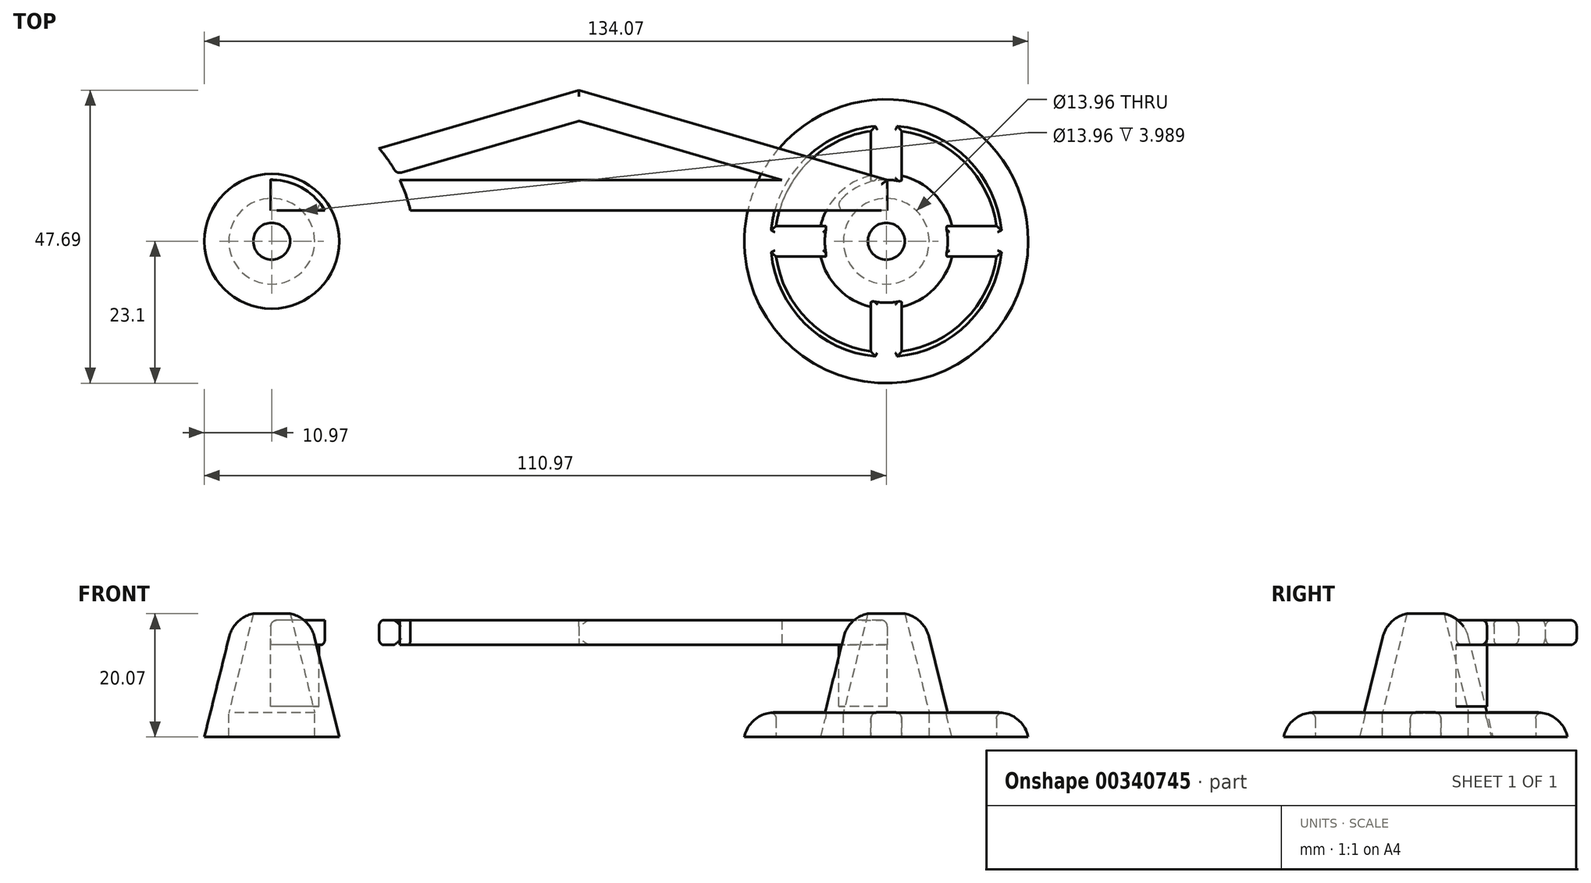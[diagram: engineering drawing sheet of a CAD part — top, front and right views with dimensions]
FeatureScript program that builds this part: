
annotation { "Feature Type Name" : "Feature", "Feature Type Description" : "" }
export const myFeature = defineFeature(function(context is Context, id is Id, definition is map)
    precondition{}
    {
        {
            var Q0;
            Q0=qCreatedBy(makeId("Top.planeOp"),FACE);
            cPlane(context, id + "F0", {"entities" : qUnion([Q0]), "cplaneType" : CPlaneType.OFFSET, "offset" : 15 * mm, "width" : 150 * mm, "height" : 150 * mm});
        }
        {
            var Q0;
            Q0=qCreatedBy(makeId("Top.planeOp"),FACE);
            var sketch = newSketch(context, id + "F1", { "sketchPlane" : qUnion([Q0])});
            skCircle(sketch, "E0", {"center": v(50, 0) * mm, "radius": 23.1 * mm});
            skCircle(sketch, "E1", {"center": v(50, 0) * mm, "radius": 10 * mm});
            skCircle(sketch, "E2", {"center": v(50, 0) * mm, "radius": 4 * mm});
            skCircle(sketch, "E3.MirrorC", {"center": v(-50, 0) * mm, "radius": 23.1 * mm});
            skCircle(sketch, "E4.MirrorC", {"center": v(-50, 0) * mm, "radius": 10 * mm});
            skCircle(sketch, "E5.MirrorC", {"center": v(-50, 0) * mm, "radius": 4 * mm});
            skLineSegment(sketch, "E6", {"start": v(-50, -31.38) * mm, "end": v(-50, 39.18) * mm, "construction": true});
            skLineSegment(sketch, "E7.MirrorCS", {"start": v(50, -31.38) * mm, "end": v(50, 39.18) * mm, "construction": true});
            skLineSegment(sketch, "E8", {"start": v(-50.17, 39.18) * mm, "end": v(-50.17, 34.18) * mm, "construction": true});
            skLineSegment(sketch, "E9", {"start": v(50.17, 34.18) * mm, "end": v(50.17, 39.18) * mm, "construction": true});
            skLineSegment(sketch, "E10", {"start": v(-75.35, 0) * mm, "end": v(75.15, 0) * mm, "construction": true});
            skLineSegment(sketch, "E11", {"start": v(59.68, 2.5) * mm, "end": v(67.93, 2.5) * mm});
            skLineSegment(sketch, "E12", {"start": v(59.68, -2.5) * mm, "end": v(67.93, -2.5) * mm});
            skLineSegment(sketch, "E13", {"start": v(40.32, -2.5) * mm, "end": v(32.07, -2.5) * mm});
            skLineSegment(sketch, "E14", {"start": v(40.32, 2.5) * mm, "end": v(32.07, 2.5) * mm});
            skArc(sketch, "E15", {"start": v(52.5, 17.93) * mm, "mid": v(62.8, 12.8) * mm, "end": v(67.93, 2.5) * mm});
            skArc(sketch, "E16", {"start": v(67.93, -2.5) * mm, "mid": v(62.8, -12.8) * mm, "end": v(52.5, -17.93) * mm});
            skArc(sketch, "E17", {"start": v(47.5, -17.93) * mm, "mid": v(37.2, -12.8) * mm, "end": v(32.07, -2.5) * mm});
            skArc(sketch, "E18", {"start": v(32.07, 2.5) * mm, "mid": v(37.2, 12.8) * mm, "end": v(47.5, 17.93) * mm});
            skLineSegment(sketch, "E19", {"start": v(47.5, 17.93) * mm, "end": v(47.5, 9.68) * mm});
            skLineSegment(sketch, "E20", {"start": v(52.5, 17.93) * mm, "end": v(52.5, 9.68) * mm});
            skLineSegment(sketch, "E21", {"start": v(52.5, -9.68) * mm, "end": v(52.5, -17.93) * mm});
            skLineSegment(sketch, "E22", {"start": v(47.5, -9.68) * mm, "end": v(47.5, -17.93) * mm});
            skLineSegment(sketch, "E23.MirrorCS", {"start": v(-52.5, 17.93) * mm, "end": v(-52.5, 9.68) * mm});
            skArc(sketch, "E24.MirrorCS", {"start": v(-52.5, 17.93) * mm, "mid": v(-62.8, 12.8) * mm, "end": v(-67.93, 2.5) * mm});
            skLineSegment(sketch, "E25.MirrorCS", {"start": v(-59.68, 2.5) * mm, "end": v(-67.93, 2.5) * mm});
            skLineSegment(sketch, "E26.MirrorCS", {"start": v(-59.68, -2.5) * mm, "end": v(-67.93, -2.5) * mm});
            skArc(sketch, "E27.MirrorCS", {"start": v(-67.93, -2.5) * mm, "mid": v(-62.8, -12.8) * mm, "end": v(-52.5, -17.93) * mm});
            skLineSegment(sketch, "E28.MirrorCS", {"start": v(-52.5, -9.68) * mm, "end": v(-52.5, -17.93) * mm});
            skLineSegment(sketch, "E29.MirrorCS", {"start": v(-47.5, -9.68) * mm, "end": v(-47.5, -17.93) * mm});
            skArc(sketch, "E30.MirrorCS", {"start": v(-47.5, -17.93) * mm, "mid": v(-37.2, -12.8) * mm, "end": v(-32.07, -2.5) * mm});
            skLineSegment(sketch, "E31.MirrorCS", {"start": v(-40.32, -2.5) * mm, "end": v(-32.07, -2.5) * mm});
            skLineSegment(sketch, "E32.MirrorCS", {"start": v(-40.32, 2.5) * mm, "end": v(-32.07, 2.5) * mm});
            skArc(sketch, "E33.MirrorCS", {"start": v(-32.07, 2.5) * mm, "mid": v(-37.2, 12.8) * mm, "end": v(-47.5, 17.93) * mm});
            skLineSegment(sketch, "E34.MirrorCS", {"start": v(-47.5, 17.93) * mm, "end": v(-47.5, 9.68) * mm});
            skSolve(sketch);
        }
        {
            var Q0;
            Q0=qCreatedBy(makeId("Front.planeOp"),FACE);
            var sketch = newSketch(context, id + "F2", { "sketchPlane" : qUnion([Q0])});
            skLineSegment(sketch, "E35", {"start": v(50, 20.07) * mm, "end": v(50, 0) * mm});
            skLineSegment(sketch, "E36", {"start": v(50, 20.07) * mm, "end": v(56, 20.07) * mm});
            skLineSegment(sketch, "E37", {"start": v(56, 20.07) * mm, "end": v(59.98, 3.99) * mm});
            skLineSegment(sketch, "E38", {"start": v(59.98, 3.99) * mm, "end": v(50, 3.99) * mm});
            skLineSegment(sketch, "E39", {"start": v(50, 3.99) * mm, "end": v(59.98, 3.99) * mm});
            skLineSegment(sketch, "E40", {"start": v(50, 0) * mm, "end": v(59.98, 0) * mm});
            skLineSegment(sketch, "E41", {"start": v(59.98, 0) * mm, "end": v(59.98, 3.99) * mm});
            skLineSegment(sketch, "E42", {"start": v(53, 20.07) * mm, "end": v(56.98, 3.99) * mm});
            skLineSegment(sketch, "E43", {"start": v(56.98, 3.99) * mm, "end": v(56.98, 0) * mm});
            skLineSegment(sketch, "E44", {"start": v(59.98, 3.99) * mm, "end": v(60.97, 0) * mm});
            skLineSegment(sketch, "E45", {"start": v(60.97, 0) * mm, "end": v(59.98, 0) * mm});
            skLineSegment(sketch, "E46.MirrorCS", {"start": v(-50, 20.07) * mm, "end": v(-56, 20.07) * mm});
            skLineSegment(sketch, "E47.MirrorCS", {"start": v(-59.98, 3.99) * mm, "end": v(-60.97, 0) * mm});
            skLineSegment(sketch, "E48.MirrorCS", {"start": v(-60.97, 0) * mm, "end": v(-59.98, 0) * mm});
            skLineSegment(sketch, "E49.MirrorCS", {"start": v(-59.98, 0) * mm, "end": v(-59.98, 3.99) * mm});
            skLineSegment(sketch, "E50.MirrorCS", {"start": v(-50, 0) * mm, "end": v(-59.98, 0) * mm});
            skLineSegment(sketch, "E51.MirrorCS", {"start": v(-50, 3.99) * mm, "end": v(-59.98, 3.99) * mm});
            skLineSegment(sketch, "E52.MirrorCS", {"start": v(-56.98, 3.99) * mm, "end": v(-56.98, 0) * mm});
            skLineSegment(sketch, "E53.MirrorCS", {"start": v(-53, 20.07) * mm, "end": v(-56.98, 3.99) * mm});
            skLineSegment(sketch, "E54.MirrorCS", {"start": v(-50, 20.07) * mm, "end": v(-50, 0) * mm});
            skLineSegment(sketch, "E55.MirrorCS", {"start": v(-56, 20.07) * mm, "end": v(-59.98, 3.99) * mm});
            skSolve(sketch);
        }
        {
            var Q0;
            Q0=qCreatedBy(id+"F0.planeOp",FACE);
            var sketch = newSketch(context, id + "F3", { "sketchPlane" : qUnion([Q0])});
            skCircle(sketch, "E56", {"center": v(50, 0) * mm, "radius": 23.1 * mm});
            skCircle(sketch, "E57", {"center": v(50, 0) * mm, "radius": 10 * mm});
            skCircle(sketch, "E58", {"center": v(50, 0) * mm, "radius": 4 * mm});
            skCircle(sketch, "E59.MirrorC", {"center": v(-50, 0) * mm, "radius": 23.1 * mm});
            skCircle(sketch, "E60.MirrorC", {"center": v(-50, 0) * mm, "radius": 10 * mm});
            skCircle(sketch, "E61.MirrorC", {"center": v(-50, 0) * mm, "radius": 4 * mm});
            skLineSegment(sketch, "E62", {"start": v(-50.17, -31.38) * mm, "end": v(-50.17, 39.18) * mm, "construction": true});
            skLineSegment(sketch, "E63.MirrorCS", {"start": v(50.17, -31.38) * mm, "end": v(50.17, 39.18) * mm, "construction": true});
            skLineSegment(sketch, "E64", {"start": v(-50.17, 10) * mm, "end": v(50.17, 39.18) * mm, "construction": true});
            skLineSegment(sketch, "E65", {"start": v(50.17, 10) * mm, "end": v(-50.17, 39.18) * mm, "construction": true});
            skLineSegment(sketch, "E66", {"start": v(50.17, 10) * mm, "end": v(-50.17, 10) * mm, "construction": true});
            skLineSegment(sketch, "E67.0", {"start": v(50.17, 5) * mm, "end": v(-50.17, 5) * mm, "construction": true});
            skLineSegment(sketch, "E68", {"start": v(-50.17, 39.18) * mm, "end": v(-50.17, 34.18) * mm, "construction": true});
            skLineSegment(sketch, "E69", {"start": v(50.17, 34.18) * mm, "end": v(50.17, 39.18) * mm, "construction": true});
            skLineSegment(sketch, "E70", {"start": v(-50.17, 34.18) * mm, "end": v(50.17, 5) * mm, "construction": true});
            skLineSegment(sketch, "E71", {"start": v(50.17, 34.18) * mm, "end": v(-50.17, 5) * mm, "construction": true});
            skLineSegment(sketch, "E72", {"start": v(-32.97, 10) * mm, "end": v(0, 19.59) * mm});
            skLineSegment(sketch, "E73", {"start": v(0, 19.59) * mm, "end": v(32.97, 10) * mm});
            skLineSegment(sketch, "E74", {"start": v(32.97, 10) * mm, "end": v(-32.97, 10) * mm});
            skLineSegment(sketch, "E75", {"start": v(-50.17, 10) * mm, "end": v(0, 24.59) * mm});
            skLineSegment(sketch, "E76", {"start": v(0, 24.59) * mm, "end": v(50.17, 10) * mm});
            skLineSegment(sketch, "E77", {"start": v(50.17, 10) * mm, "end": v(50.17, 5) * mm});
            skLineSegment(sketch, "E78", {"start": v(50.17, 5) * mm, "end": v(-50.17, 5) * mm});
            skLineSegment(sketch, "E79", {"start": v(-50.17, 5) * mm, "end": v(-50.17, 10) * mm});
            skSolve(sketch);
        }
        {
            var Q0;
            {var subQ0=sQuery(id+"F2.wireOp",EDGE,"E37");Q0=makeQuery(id+"F2.imprint","IMPRINT",FACE,{"disambiguationData":[TD([[makeQuery(id+"F2.imprint","IMPRINT",EDGE,{"derivedFrom":subQ0}),-1.0]])]});}
            var Q1;
            {var subQ0=sQuery(id+"F2.wireOp",EDGE,"E41");Q1=makeQuery(id+"F2.imprint","IMPRINT",FACE,{"disambiguationData":[TD([[makeQuery(id+"F2.imprint","IMPRINT",EDGE,{"derivedFrom":subQ0}),1.0]])]});}
            var Q2;
            Q2=makeQuery(id+"F2.imprint","IMPRINT",FACE,{"disambiguationData":[TD([[makeQuery(id+"F2.imprint","IMPRINT",EDGE,{"derivedFrom":sQuery(id+"F2.wireOp",EDGE,"E41")}),-1.0]])]});
            var Q3;
            Q3=sQuery(id+"F2.wireOp",EDGE,"E35");
            revolve(context, id + "F4", {"entities" : qUnion([Q0, Q1, Q2]), "axis" : qUnion([Q3]), "revolveType" : RevolveType.FULL});
        }
        {
            var Q0;
            {var subQ2=sQuery(id+"F2.wireOp",EDGE,"E53.MirrorCS");Q0=makeQuery(id+"F2.imprint","IMPRINT",FACE,{"disambiguationData":[TD([[makeQuery(id+"F2.imprint","IMPRINT",EDGE,{"derivedFrom":subQ2}),-1.0]])]});}
            var Q1;
            Q1=makeQuery(id+"F2.imprint","IMPRINT",FACE,{"disambiguationData":[TD([[makeQuery(id+"F2.imprint","IMPRINT",EDGE,{"derivedFrom":sQuery(id+"F2.wireOp",EDGE,"E47.MirrorCS")}),1.0]])]});
            var Q2;
            {var subQ0=sQuery(id+"F2.wireOp",EDGE,"E49.MirrorCS");Q2=makeQuery(id+"F2.imprint","IMPRINT",FACE,{"disambiguationData":[TD([[makeQuery(id+"F2.imprint","IMPRINT",EDGE,{"derivedFrom":subQ0}),-1.0]])]});}
            var Q3;
            Q3=sQuery(id+"F2.wireOp",EDGE,"E54.MirrorCS");
            revolve(context, id + "F5", {"entities" : qUnion([Q0, Q1, Q2]), "axis" : qUnion([Q3]), "revolveType" : RevolveType.FULL});
        }
        {
            var Q0;
            Q0=makeQuery(id+"F1.imprint","IMPRINT",FACE,{"disambiguationData":[TD([[makeQuery(id+"F1.imprint","IMPRINT",EDGE,{"derivedFrom":sQuery(id+"F1.wireOp",EDGE,"E0")}),1.0]])]});
            var Q1;
            Q1=makeQuery(id+"F1.imprint","IMPRINT",FACE,{"disambiguationData":[TD([[makeQuery(id+"F1.imprint","IMPRINT",EDGE,{"derivedFrom":sQuery(id+"F1.wireOp",EDGE,"E3.MirrorC")}),-1.0]])]});
            extrude(context, id + "F6", {"entities" : qUnion([Q0, Q1]), "operationType" : NewBodyOperationType.ADD, "depth" : 4 * mm});
        }
        {
            var Q0;
            {var subQ0=sQuery(id+"F3.wireOp",EDGE,"E76");var subQ8=sQuery(id+"F3.wireOp",EDGE,"E56");var subQ12=makeQuery(id+"F3.imprint","INTERSECT",VERTEX,{"derivedFrom":[subQ8,subQ0]});Q0=makeQuery(id+"F3.imprint","IMPRINT",FACE,{"disambiguationData":[TD([[makeQuery(id+"F3.imprint","IMPRINT",EDGE,{"disambiguationData":[TD([[subQ12,-1.0]])],"derivedFrom":subQ8}),1.0]])]});}
            var Q1;
            {var subQ0=sQuery(id+"F3.wireOp",EDGE,"E78");var subQ1=sQuery(id+"F3.wireOp",EDGE,"E56");var subQ2=makeQuery(id+"F3.imprint","INTERSECT",VERTEX,{"derivedFrom":[subQ1,subQ0]});Q1=makeQuery(id+"F3.imprint","IMPRINT",FACE,{"disambiguationData":[TD([[makeQuery(id+"F3.imprint","IMPRINT",EDGE,{"disambiguationData":[TD([[subQ2,1.0]])],"derivedFrom":subQ1}),-1.0]])]});}
            var Q2;
            {var subQ0=sQuery(id+"F3.wireOp",EDGE,"E75");var subQ8=sQuery(id+"F3.wireOp",EDGE,"E59.MirrorC");var subQ12=makeQuery(id+"F3.imprint","INTERSECT",VERTEX,{"derivedFrom":[subQ8,subQ0]});Q2=makeQuery(id+"F3.imprint","IMPRINT",FACE,{"disambiguationData":[TD([[makeQuery(id+"F3.imprint","IMPRINT",EDGE,{"disambiguationData":[TD([[subQ12,-1.0]])],"derivedFrom":subQ8}),-1.0]])]});}
            var Q3;
            {var subQ3=sQuery(id+"F3.wireOp",EDGE,"E56");var subQ9=sQuery(id+"F3.wireOp",EDGE,"E76");var subQ10=makeQuery(id+"F3.imprint","INTERSECT",VERTEX,{"derivedFrom":[subQ3,subQ9]});Q3=makeQuery(id+"F3.imprint","IMPRINT",FACE,{"disambiguationData":[TD([[makeQuery(id+"F3.imprint","IMPRINT",EDGE,{"disambiguationData":[TD([[subQ10,-1.0]])],"derivedFrom":subQ3}),-1.0]])]});}
            var Q4;
            {var subQ0=sQuery(id+"F3.wireOp",EDGE,"E77");Q4=makeQuery(id+"F3.imprint","IMPRINT",FACE,{"disambiguationData":[TD([[makeQuery(id+"F3.imprint","IMPRINT",EDGE,{"derivedFrom":subQ0}),-1.0]])]});}
            var Q5;
            {var subQ0=sQuery(id+"F3.wireOp",EDGE,"E79");Q5=makeQuery(id+"F3.imprint","IMPRINT",FACE,{"disambiguationData":[TD([[makeQuery(id+"F3.imprint","IMPRINT",EDGE,{"derivedFrom":subQ0}),-1.0]])]});}
            extrude(context, id + "F7", {"entities" : qUnion([Q0, Q1, Q2, Q3, Q4, Q5]), "depth" : 4 * mm});
        }
        {
            var Q0;
            Q0=makeQuery(id+"F4.opRevolve","SWEPT_EDGE",EDGE,{"disambiguationData":[OSD([sQuery(id+"F2.wireOp",EDGE,"E36"),sQuery(id+"F2.wireOp",EDGE,"E37")])]});
            var Q1;
            Q1=makeQuery(id+"F6.opExtrude","CAP_EDGE",EDGE,{"disambiguationData":[OSD([sQuery(id+"F1.wireOp",EDGE,"E0")])],"isStart":false});
            var Q2;
            Q2=makeQuery(id+"F5.opRevolve","SWEPT_EDGE",EDGE,{"disambiguationData":[OSD([sQuery(id+"F2.wireOp",EDGE,"E46.MirrorCS"),sQuery(id+"F2.wireOp",EDGE,"E55.MirrorCS")])]});
            var Q3;
            Q3=makeQuery(id+"F6.opExtrude","CAP_EDGE",EDGE,{"disambiguationData":[OSD([sQuery(id+"F1.wireOp",EDGE,"E3.MirrorC")])],"isStart":false});
            fillet(context, id + "F8", {"entities" : qUnion([Q0, Q1, Q2, Q3]), "radius" : 5 * mm, "tangentPropagation" : true, "allowEdgeOverflow" : false});
        }
        {
            var Q0;
            {var subQ0=sQuery(id+"F3.wireOp",EDGE,"E79");Q0=makeQuery(id+"F3.imprint","IMPRINT",FACE,{"disambiguationData":[TD([[makeQuery(id+"F3.imprint","IMPRINT",EDGE,{"derivedFrom":subQ0}),-1.0]])]});}
            var Q1;
            {var subQ0=sQuery(id+"F3.wireOp",EDGE,"E77");Q1=makeQuery(id+"F3.imprint","IMPRINT",FACE,{"disambiguationData":[TD([[makeQuery(id+"F3.imprint","IMPRINT",EDGE,{"derivedFrom":subQ0}),-1.0]])]});}
            extrude(context, id + "F9", {"entities" : qUnion([Q0, Q1]), "depth" : -10 * mm});
        }
        {
            var Q0;
            Q0=makeQuery(id+"F7.opExtrude","CAP_EDGE",EDGE,{"disambiguationData":[OSD([sQuery(id+"F3.wireOp",EDGE,"E76")])],"isStart":true});
            var Q1;
            Q1=makeQuery(id+"F7.opExtrude","CAP_EDGE",EDGE,{"disambiguationData":[OSD([sQuery(id+"F3.wireOp",EDGE,"E75")])],"isStart":true});
            var Q2;
            Q2=makeQuery(id+"F7.opExtrude","CAP_EDGE",EDGE,{"disambiguationData":[OSD([sQuery(id+"F3.wireOp",EDGE,"E75")])],"isStart":false});
            var Q3;
            Q3=makeQuery(id+"F7.opExtrude","CAP_EDGE",EDGE,{"disambiguationData":[OSD([sQuery(id+"F3.wireOp",EDGE,"E76")])],"isStart":false});
            var Q4;
            Q4=makeQuery(id+"F7.opExtrude","SWEPT_FACE",FACE,{"disambiguationData":[OSD([sQuery(id+"F3.wireOp",EDGE,"E72")])]});
            var Q5;
            Q5=makeQuery(id+"F9.opExtrude","SWEPT_EDGE",EDGE,{"disambiguationData":[OSD([sQuery(id+"F3.wireOp",EDGE,"E57"),sQuery(id+"F3.wireOp",EDGE,"E78")])]});
            var Q6;
            Q6=makeQuery(id+"F7.opExtrude","CAP_EDGE",EDGE,{"disambiguationData":[OSD([sQuery(id+"F3.wireOp",EDGE,"E78")])],"isStart":true});
            var Q7;
            Q7=makeQuery(id+"F9.opExtrude","SWEPT_EDGE",EDGE,{"disambiguationData":[OSD([sQuery(id+"F3.wireOp",EDGE,"E60.MirrorC"),sQuery(id+"F3.wireOp",EDGE,"E78")])]});
            var Q8;
            Q8=makeQuery(id+"F7.opExtrude","CAP_EDGE",EDGE,{"disambiguationData":[OSD([sQuery(id+"F3.wireOp",EDGE,"E79")])],"isStart":false});
            var Q9;
            Q9=makeQuery(id+"F7.opExtrude","CAP_EDGE",EDGE,{"disambiguationData":[OSD([sQuery(id+"F3.wireOp",EDGE,"E77")])],"isStart":false});
            var Q10;
            Q10=makeQuery(id+"F6.opExtrude","CAP_FACE",FACE,{"disambiguationData":[OSD([sQuery(id+"F1.wireOp",EDGE,"E3.MirrorC"),sQuery(id+"F1.wireOp",EDGE,"E4.MirrorC"),sQuery(id+"F1.wireOp",EDGE,"E23.MirrorCS"),sQuery(id+"F1.wireOp",EDGE,"E24.MirrorCS"),sQuery(id+"F1.wireOp",EDGE,"E25.MirrorCS"),sQuery(id+"F1.wireOp",EDGE,"E26.MirrorCS"),sQuery(id+"F1.wireOp",EDGE,"E27.MirrorCS"),sQuery(id+"F1.wireOp",EDGE,"E28.MirrorCS"),sQuery(id+"F1.wireOp",EDGE,"E29.MirrorCS"),sQuery(id+"F1.wireOp",EDGE,"E30.MirrorCS"),sQuery(id+"F1.wireOp",EDGE,"E31.MirrorCS"),sQuery(id+"F1.wireOp",EDGE,"E32.MirrorCS"),sQuery(id+"F1.wireOp",EDGE,"E33.MirrorCS"),sQuery(id+"F1.wireOp",EDGE,"E34.MirrorCS")])],"isStart":false});
            var Q11;
            Q11=makeQuery(id+"F6.opExtrude","CAP_FACE",FACE,{"disambiguationData":[OSD([sQuery(id+"F1.wireOp",EDGE,"E0"),sQuery(id+"F1.wireOp",EDGE,"E1"),sQuery(id+"F1.wireOp",EDGE,"E15"),sQuery(id+"F1.wireOp",EDGE,"E16"),sQuery(id+"F1.wireOp",EDGE,"E17"),sQuery(id+"F1.wireOp",EDGE,"E18"),sQuery(id+"F1.wireOp",EDGE,"E19"),sQuery(id+"F1.wireOp",EDGE,"E20"),sQuery(id+"F1.wireOp",EDGE,"E11"),sQuery(id+"F1.wireOp",EDGE,"E12"),sQuery(id+"F1.wireOp",EDGE,"E21"),sQuery(id+"F1.wireOp",EDGE,"E22"),sQuery(id+"F1.wireOp",EDGE,"E13"),sQuery(id+"F1.wireOp",EDGE,"E14")])],"isStart":false});
            fillet(context, id + "F10", {"entities" : qUnion([Q0, Q1, Q2, Q3, Q4, Q5, Q6, Q7, Q8, Q9, Q10, Q11]), "radius" : 1 * mm, "tangentPropagation" : true, "allowEdgeOverflow" : false});
        }
    });
